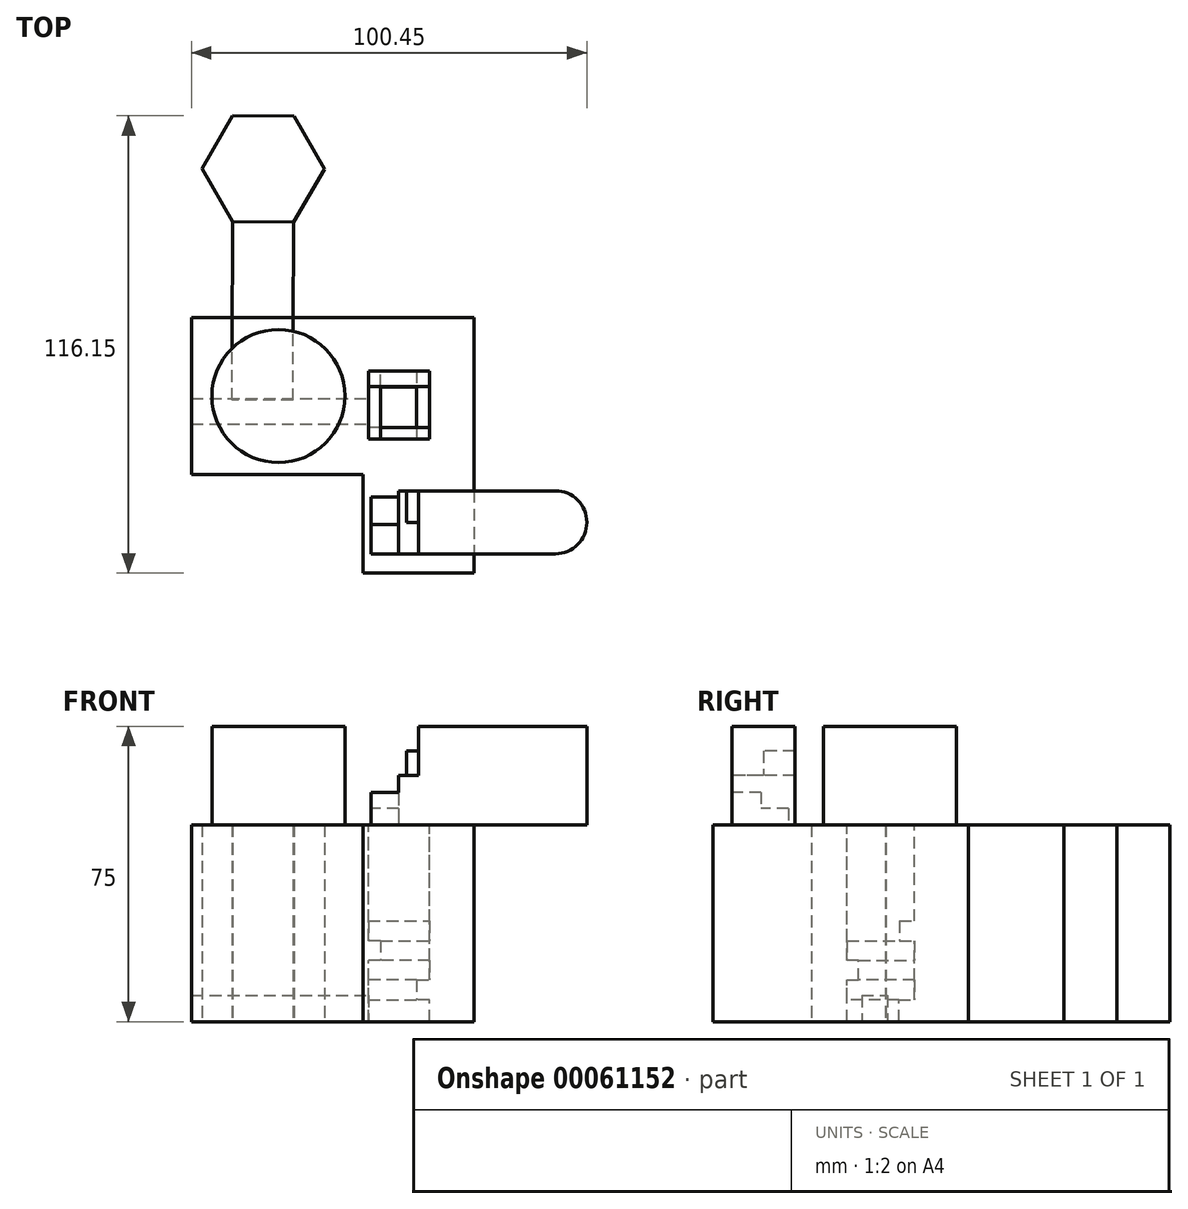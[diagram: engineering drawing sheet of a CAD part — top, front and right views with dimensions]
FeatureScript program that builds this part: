
annotation { "Feature Type Name" : "Feature", "Feature Type Description" : "" }
export const myFeature = defineFeature(function(context is Context, id is Id, definition is map)
    precondition{}
    {
        {
            var Q0;
            Q0=qCreatedBy(makeId("Top.planeOp"),FACE);
            var sketch = newSketch(context, id + "F0", { "sketchPlane" : qUnion([Q0])});
            skLineSegment(sketch, "E0.bottom", {"start": v(-25.79, 13.66) * mm, "end": v(46.05, 13.66) * mm});
            skLineSegment(sketch, "E0.top", {"start": v(-25.79, -26.25) * mm, "end": v(46.05, -26.25) * mm});
            skLineSegment(sketch, "E0.left", {"start": v(-25.79, 13.66) * mm, "end": v(-25.79, -26.25) * mm});
            skLineSegment(sketch, "E0.right", {"start": v(46.05, 13.66) * mm, "end": v(46.05, -26.25) * mm});
            skSolve(sketch);
        }
        {
            var Q0;
            Q0=qSketchRegion(id+"F0",true);
            extrude(context, id + "F1", {"entities" : qUnion([Q0]), "depth" : 25 * mm, "hasSecondDirection" : true, "secondDirectionOppositeDirection" : true, "secondDirectionDepth" : 25 * mm});
        }
        {
            var Q0;
            Q0=makeQuery(id+"F1.opExtrude","CAP_FACE",FACE,{"disambiguationData":[OSD([sQuery(id+"F0.wireOp",EDGE,"E0.bottom"),sQuery(id+"F0.wireOp",EDGE,"E0.top"),sQuery(id+"F0.wireOp",EDGE,"E0.left"),sQuery(id+"F0.wireOp",EDGE,"E0.right")])],"isStart":false});
            var sketch = newSketch(context, id + "F2", { "sketchPlane" : qUnion([Q0])});
            skLineSegment(sketch, "E1.bottom", {"start": v(19.18, 0) * mm, "end": v(34.73, 0) * mm});
            skLineSegment(sketch, "E1.top", {"start": v(19.18, -17.18) * mm, "end": v(34.73, -17.18) * mm});
            skLineSegment(sketch, "E1.left", {"start": v(19.18, 0) * mm, "end": v(19.18, -17.18) * mm});
            skLineSegment(sketch, "E1.right", {"start": v(34.73, 0) * mm, "end": v(34.73, -17.18) * mm});
            skSolve(sketch);
        }
        {
            var Q0;
            Q0=makeQuery(id+"F1.opExtrude","SWEPT_FACE",FACE,{"disambiguationData":[OSD([sQuery(id+"F0.wireOp",EDGE,"E0.top")])]});
            var sketch = newSketch(context, id + "F3", { "sketchPlane" : qUnion([Q0])});
            skLineSegment(sketch, "E2.bottom", {"start": v(46.05, 25) * mm, "end": v(17.8, 25) * mm});
            skLineSegment(sketch, "E2.top", {"start": v(46.05, -25) * mm, "end": v(17.8, -25) * mm});
            skLineSegment(sketch, "E2.left", {"start": v(46.05, 25) * mm, "end": v(46.05, -25) * mm});
            skLineSegment(sketch, "E2.right", {"start": v(17.8, 25) * mm, "end": v(17.8, -25) * mm});
            skSolve(sketch);
        }
        {
            var Q0;
            Q0=qSketchRegion(id+"F3",true);
            extrude(context, id + "F4", {"entities" : qUnion([Q0]), "operationType" : NewBodyOperationType.ADD, "depth" : 25 * mm});
        }
        {
            var Q0;
            Q0=makeQuery(id+"F2.imprint","IMPRINT",FACE,{"disambiguationData":[TD([[makeQuery(id+"F2.imprint","IMPRINT",EDGE,{"derivedFrom":sQuery(id+"F2.wireOp",EDGE,"E1.bottom")}),-1.0]])]});
            var Q1;
            Q1=qSketchRegion(id+"F2",true);
            extrude(context, id + "F5", {"entities" : qUnion([Q0, Q1]), "operationType" : NewBodyOperationType.REMOVE, "endBound" : BoundingType.THROUGH_ALL, "oppositeDirection" : true, "depth" : 25 * mm});
        }
        {
            var Q0;
            Q0=makeQuery(id+"F4.boolean.opBoolean","MERGE",FACE,{"derivedFrom":[makeQuery(id+"F1.opExtrude","CAP_FACE",FACE,{"disambiguationData":[OSD([sQuery(id+"F0.wireOp",EDGE,"E0.bottom"),sQuery(id+"F0.wireOp",EDGE,"E0.top"),sQuery(id+"F0.wireOp",EDGE,"E0.left"),sQuery(id+"F0.wireOp",EDGE,"E0.right")])],"isStart":false}),makeQuery(id+"F4.opExtrude","SWEPT_FACE",FACE,{"disambiguationData":[OSD([sQuery(id+"F3.wireOp",EDGE,"E2.bottom")])]})]});
            var sketch = newSketch(context, id + "F6", { "sketchPlane" : qUnion([Q0])});
            skCircle(sketch, "E3", {"center": v(-3.68, -6.3) * mm, "radius": 16.9 * mm});
            skSolve(sketch);
        }
        {
            var Q0;
            Q0=makeQuery(id+"F6.imprint","IMPRINT",FACE,{"disambiguationData":[TD([[makeQuery(id+"F6.imprint","IMPRINT",EDGE,{"derivedFrom":sQuery(id+"F6.wireOp",EDGE,"E3")}),1.0]])]});
            extrude(context, id + "F7", {"entities" : qUnion([Q0]), "operationType" : NewBodyOperationType.ADD, "depth" : 25 * mm});
        }
        {
            var Q0;
            Q0=makeQuery(id+"F4.boolean.opBoolean","MERGE",FACE,{"derivedFrom":[makeQuery(id+"F1.opExtrude","CAP_FACE",FACE,{"disambiguationData":[OSD([sQuery(id+"F0.wireOp",EDGE,"E0.bottom"),sQuery(id+"F0.wireOp",EDGE,"E0.top"),sQuery(id+"F0.wireOp",EDGE,"E0.left"),sQuery(id+"F0.wireOp",EDGE,"E0.right")])],"isStart":false}),makeQuery(id+"F4.opExtrude","SWEPT_FACE",FACE,{"disambiguationData":[OSD([sQuery(id+"F3.wireOp",EDGE,"E2.bottom")])]})]});
            var sketch = newSketch(context, id + "F8", { "sketchPlane" : qUnion([Q0])});
            skLineSegment(sketch, "E4", {"start": v(31.87, -30.37) * mm, "end": v(66.65, -30.37) * mm});
            skLineSegment(sketch, "E5", {"start": v(31.87, -46.4) * mm, "end": v(66.65, -46.4) * mm});
            skArc(sketch, "E6", {"start": v(66.65, -46.4) * mm, "mid": v(74.66, -38.38) * mm, "end": v(66.65, -30.37) * mm});
            skLineSegment(sketch, "E7", {"start": v(31.87, -46.4) * mm, "end": v(31.87, -30.37) * mm});
            skSolve(sketch);
        }
        {
            var Q0;
            {var subQ0=sQuery(id+"F8.wireOp",EDGE,"E6");Q0=makeQuery(id+"F8.imprint","IMPRINT",FACE,{"disambiguationData":[TD([[makeQuery(id+"F8.imprint","IMPRINT",EDGE,{"derivedFrom":subQ0}),1.0]])]});}
            var Q1;
            {var subQ0=sQuery(id+"F8.wireOp",EDGE,"E7");Q1=makeQuery(id+"F8.imprint","IMPRINT",FACE,{"disambiguationData":[TD([[makeQuery(id+"F8.imprint","IMPRINT",EDGE,{"derivedFrom":subQ0}),-1.0]])]});}
            extrude(context, id + "F9", {"entities" : qUnion([Q0, Q1]), "operationType" : NewBodyOperationType.ADD, "depth" : 25 * mm});
        }
        {
            var Q0;
            Q0=makeQuery(id+"F9.opExtrude","SWEPT_FACE",FACE,{"disambiguationData":[OSD([sQuery(id+"F8.wireOp",EDGE,"E7")])]});
            var sketch = newSketch(context, id + "F10", { "sketchPlane" : qUnion([Q0])});
            skLineSegment(sketch, "E8.bottom", {"start": v(30.37, 37.5) * mm, "end": v(46.4, 37.5) * mm});
            skLineSegment(sketch, "E8.top", {"start": v(30.37, 25) * mm, "end": v(46.4, 25) * mm});
            skLineSegment(sketch, "E8.left", {"start": v(30.37, 37.5) * mm, "end": v(30.37, 25) * mm});
            skLineSegment(sketch, "E8.right", {"start": v(46.4, 37.5) * mm, "end": v(46.4, 25) * mm});
            skSolve(sketch);
        }
        {
            var Q0;
            Q0=makeQuery(id+"F10.imprint","IMPRINT",FACE,{"disambiguationData":[TD([[makeQuery(id+"F10.imprint","IMPRINT",EDGE,{"derivedFrom":sQuery(id+"F10.wireOp",EDGE,"E8.bottom")}),-1.0]])]});
            extrude(context, id + "F11", {"entities" : qUnion([Q0]), "operationType" : NewBodyOperationType.ADD, "depth" : 5 * mm});
        }
        {
            var Q0;
            Q0=makeQuery(id+"F11.opExtrude","CAP_FACE",FACE,{"disambiguationData":[OSD([sQuery(id+"F10.wireOp",EDGE,"E8.bottom"),sQuery(id+"F10.wireOp",EDGE,"E8.top"),sQuery(id+"F10.wireOp",EDGE,"E8.left"),sQuery(id+"F10.wireOp",EDGE,"E8.right")])],"isStart":false});
            var sketch = newSketch(context, id + "F12", { "sketchPlane" : qUnion([Q0])});
            skLineSegment(sketch, "E9.bottom", {"start": v(38.97, 33.28) * mm, "end": v(46.4, 33.28) * mm});
            skLineSegment(sketch, "E9.top", {"start": v(38.97, 25) * mm, "end": v(46.4, 25) * mm});
            skLineSegment(sketch, "E9.left", {"start": v(38.97, 33.28) * mm, "end": v(38.97, 25) * mm});
            skLineSegment(sketch, "E9.right", {"start": v(46.4, 33.28) * mm, "end": v(46.4, 25) * mm});
            skSolve(sketch);
        }
        {
            var Q0;
            Q0=qSketchRegion(id+"F12",true);
            extrude(context, id + "F13", {"entities" : qUnion([Q0]), "operationType" : NewBodyOperationType.ADD, "depth" : 7 * mm});
        }
        {
            var Q0;
            Q0=makeQuery(id+"F13.opExtrude","SWEPT_FACE",FACE,{"disambiguationData":[OSD([sQuery(id+"F12.wireOp",EDGE,"E9.left")])]});
            var sketch = newSketch(context, id + "F14", { "sketchPlane" : qUnion([Q0])});
            skLineSegment(sketch, "E10.bottom", {"start": v(-26.87, 29.14) * mm, "end": v(-19.87, 29.14) * mm});
            skLineSegment(sketch, "E10.top", {"start": v(-26.87, 25) * mm, "end": v(-19.87, 25) * mm});
            skLineSegment(sketch, "E10.left", {"start": v(-26.87, 29.14) * mm, "end": v(-26.87, 25) * mm});
            skLineSegment(sketch, "E10.right", {"start": v(-19.87, 29.14) * mm, "end": v(-19.87, 25) * mm});
            skSolve(sketch);
        }
        {
            var Q0;
            Q0=qSketchRegion(id+"F14",true);
            extrude(context, id + "F15", {"entities" : qUnion([Q0]), "operationType" : NewBodyOperationType.ADD, "depth" : 7 * mm});
        }
        {
            var Q0;
            Q0=makeQuery(id+"F9.opExtrude","SWEPT_FACE",FACE,{"disambiguationData":[OSD([sQuery(id+"F8.wireOp",EDGE,"E7")])]});
            var sketch = newSketch(context, id + "F16", { "sketchPlane" : qUnion([Q0])});
            skLineSegment(sketch, "E11.bottom", {"start": v(30.37, 43.75) * mm, "end": v(38.38, 43.75) * mm});
            skLineSegment(sketch, "E11.top", {"start": v(30.37, 37.5) * mm, "end": v(38.38, 37.5) * mm});
            skLineSegment(sketch, "E11.left", {"start": v(30.37, 43.75) * mm, "end": v(30.37, 37.5) * mm});
            skLineSegment(sketch, "E11.right", {"start": v(38.38, 43.75) * mm, "end": v(38.38, 37.5) * mm});
            skSolve(sketch);
        }
        {
            var Q0;
            Q0=qSketchRegion(id+"F16",true);
            extrude(context, id + "F17", {"entities" : qUnion([Q0]), "operationType" : NewBodyOperationType.ADD, "depth" : 3 * mm});
        }
        {
            var Q0;
            Q0=makeQuery(id+"F5.boolean.opBoolean","COPY",FACE,{"derivedFrom":makeQuery(id+"F5.opExtrude","SWEPT_FACE",FACE,{"disambiguationData":[OSD([sQuery(id+"F2.wireOp",EDGE,"E1.bottom")])]})});
            var sketch = newSketch(context, id + "F18", { "sketchPlane" : qUnion([Q0])});
            skLineSegment(sketch, "E12.bottom", {"start": v(19.18, -25) * mm, "end": v(34.73, -25) * mm});
            skLineSegment(sketch, "E12.top", {"start": v(19.18, -19.44) * mm, "end": v(34.73, -19.44) * mm});
            skLineSegment(sketch, "E12.left", {"start": v(19.18, -25) * mm, "end": v(19.18, -19.44) * mm});
            skLineSegment(sketch, "E12.right", {"start": v(34.73, -25) * mm, "end": v(34.73, -19.44) * mm});
            skSolve(sketch);
        }
        {
            var Q0;
            Q0=makeQuery(id+"F18.imprint","IMPRINT",FACE,{"disambiguationData":[TD([[makeQuery(id+"F18.imprint","IMPRINT",EDGE,{"derivedFrom":sQuery(id+"F18.wireOp",EDGE,"E12.bottom")}),1.0]])]});
            extrude(context, id + "F19", {"entities" : qUnion([Q0]), "operationType" : NewBodyOperationType.ADD, "depth" : 4 * mm});
        }
        {
            var Q0;
            Q0=makeQuery(id+"F19.opExtrude","SWEPT_FACE",FACE,{"disambiguationData":[OSD([sQuery(id+"F18.wireOp",EDGE,"E12.top")])]});
            var sketch = newSketch(context, id + "F20", { "sketchPlane" : qUnion([Q0])});
            skLineSegment(sketch, "E13.bottom", {"start": v(34.73, 0) * mm, "end": v(31.43, 0) * mm});
            skLineSegment(sketch, "E13.top", {"start": v(34.73, -17.48) * mm, "end": v(31.43, -17.48) * mm});
            skLineSegment(sketch, "E13.left", {"start": v(34.73, 0) * mm, "end": v(34.73, -17.48) * mm});
            skLineSegment(sketch, "E13.right", {"start": v(31.43, 0) * mm, "end": v(31.43, -17.48) * mm});
            skSolve(sketch);
        }
        {
            var Q0;
            Q0=qSketchRegion(id+"F20",true);
            extrude(context, id + "F21", {"entities" : qUnion([Q0]), "operationType" : NewBodyOperationType.ADD, "depth" : 5 * mm});
        }
        {
            var Q0;
            Q0=makeQuery(id+"F21.opExtrude","CAP_FACE",FACE,{"disambiguationData":[OSD([sQuery(id+"F20.wireOp",EDGE,"E13.bottom"),sQuery(id+"F20.wireOp",EDGE,"E13.top"),sQuery(id+"F20.wireOp",EDGE,"E13.left"),sQuery(id+"F20.wireOp",EDGE,"E13.right")])],"isStart":false});
            var sketch = newSketch(context, id + "F22", { "sketchPlane" : qUnion([Q0])});
            skLineSegment(sketch, "E14.bottom", {"start": v(34.73, -14.24) * mm, "end": v(19.11, -14.24) * mm});
            skLineSegment(sketch, "E14.top", {"start": v(34.73, -17.18) * mm, "end": v(19.11, -17.18) * mm});
            skLineSegment(sketch, "E14.left", {"start": v(34.73, -14.24) * mm, "end": v(34.73, -17.18) * mm});
            skLineSegment(sketch, "E14.right", {"start": v(19.11, -14.24) * mm, "end": v(19.11, -17.18) * mm});
            skSolve(sketch);
        }
        {
            var Q0;
            {var subQ0=sQuery(id+"F22.wireOp",EDGE,"E14.right");Q0=makeQuery(id+"F22.imprint","IMPRINT",FACE,{"disambiguationData":[TD([[makeQuery(id+"F22.imprint","IMPRINT",EDGE,{"derivedFrom":subQ0}),1.0]])]});}
            var Q1;
            {var subQ0=sQuery(id+"F22.wireOp",EDGE,"E14.left");Q1=makeQuery(id+"F22.imprint","IMPRINT",FACE,{"disambiguationData":[TD([[makeQuery(id+"F22.imprint","IMPRINT",EDGE,{"derivedFrom":subQ0}),-1.0]])]});}
            extrude(context, id + "F23", {"entities" : qUnion([Q0, Q1]), "operationType" : NewBodyOperationType.ADD, "depth" : 5 * mm});
        }
        {
            var Q0;
            Q0=makeQuery(id+"F23.opExtrude","CAP_FACE",FACE,{"disambiguationData":[OSD([sQuery(id+"F22.wireOp",EDGE,"E14.bottom"),sQuery(id+"F22.wireOp",EDGE,"E14.top"),sQuery(id+"F22.wireOp",EDGE,"E14.left"),sQuery(id+"F22.wireOp",EDGE,"E14.right")])],"isStart":false});
            var sketch = newSketch(context, id + "F24", { "sketchPlane" : qUnion([Q0])});
            skLineSegment(sketch, "E15.bottom", {"start": v(22.25, -17.18) * mm, "end": v(19.18, -17.18) * mm});
            skLineSegment(sketch, "E15.top", {"start": v(22.25, 0) * mm, "end": v(19.18, 0) * mm});
            skLineSegment(sketch, "E15.left", {"start": v(22.25, -17.18) * mm, "end": v(22.25, 0) * mm});
            skLineSegment(sketch, "E15.right", {"start": v(19.18, -17.18) * mm, "end": v(19.18, 0) * mm});
            skSolve(sketch);
        }
        {
            var Q0;
            {var subQ0=sQuery(id+"F24.wireOp",EDGE,"E15.top");Q0=makeQuery(id+"F24.imprint","IMPRINT",FACE,{"disambiguationData":[TD([[makeQuery(id+"F24.imprint","IMPRINT",EDGE,{"derivedFrom":subQ0}),1.0]])]});}
            var Q1;
            {var subQ0=sQuery(id+"F24.wireOp",EDGE,"E15.bottom");Q1=makeQuery(id+"F24.imprint","IMPRINT",FACE,{"disambiguationData":[TD([[makeQuery(id+"F24.imprint","IMPRINT",EDGE,{"derivedFrom":subQ0}),-1.0]])]});}
            extrude(context, id + "F25", {"entities" : qUnion([Q0, Q1]), "operationType" : NewBodyOperationType.ADD, "depth" : 5 * mm});
        }
        {
            var Q0;
            Q0=makeQuery(id+"F25.opExtrude","CAP_FACE",FACE,{"disambiguationData":[OSD([sQuery(id+"F24.wireOp",EDGE,"E15.bottom"),sQuery(id+"F24.wireOp",EDGE,"E15.top"),sQuery(id+"F24.wireOp",EDGE,"E15.left"),sQuery(id+"F24.wireOp",EDGE,"E15.right")])],"isStart":false});
            var sketch = newSketch(context, id + "F26", { "sketchPlane" : qUnion([Q0])});
            skLineSegment(sketch, "E16.bottom", {"start": v(19.18, -3.84) * mm, "end": v(34.88, -3.84) * mm});
            skLineSegment(sketch, "E16.top", {"start": v(19.18, 0) * mm, "end": v(34.88, 0) * mm});
            skLineSegment(sketch, "E16.left", {"start": v(19.18, -3.84) * mm, "end": v(19.18, 0) * mm});
            skLineSegment(sketch, "E16.right", {"start": v(34.88, -3.84) * mm, "end": v(34.88, 0) * mm});
            skSolve(sketch);
        }
        {
            var Q0;
            {var subQ0=sQuery(id+"F26.wireOp",EDGE,"E16.right");Q0=makeQuery(id+"F26.imprint","IMPRINT",FACE,{"disambiguationData":[TD([[makeQuery(id+"F26.imprint","IMPRINT",EDGE,{"derivedFrom":subQ0}),1.0]])]});}
            var Q1;
            {var subQ0=sQuery(id+"F26.wireOp",EDGE,"E16.left");Q1=makeQuery(id+"F26.imprint","IMPRINT",FACE,{"disambiguationData":[TD([[makeQuery(id+"F26.imprint","IMPRINT",EDGE,{"derivedFrom":subQ0}),-1.0]])]});}
            extrude(context, id + "F27", {"entities" : qUnion([Q0, Q1]), "operationType" : NewBodyOperationType.ADD, "depth" : 5 * mm});
        }
        {
            var Q0;
            Q0=makeQuery(id+"F25.boolean.opBoolean","SPLIT",FACE,{"disambiguationData":[TD([makeQuery(id+"F4.opExtrude","SWEPT_FACE",FACE,{"disambiguationData":[OSD([sQuery(id+"F3.wireOp",EDGE,"E2.top")])]})])],"derivedFrom":makeQuery(id+"F5.boolean.opBoolean","COPY",FACE,{"derivedFrom":makeQuery(id+"F5.opExtrude","SWEPT_FACE",FACE,{"disambiguationData":[OSD([sQuery(id+"F2.wireOp",EDGE,"E1.left")])]})})});
            var sketch = newSketch(context, id + "F28", { "sketchPlane" : qUnion([Q0])});
            skLineSegment(sketch, "E17.bottom", {"start": v(-13.38, -18.35) * mm, "end": v(-6.94, -18.35) * mm});
            skLineSegment(sketch, "E17.top", {"start": v(-13.38, -25) * mm, "end": v(-6.94, -25) * mm});
            skLineSegment(sketch, "E17.left", {"start": v(-13.38, -18.35) * mm, "end": v(-13.38, -25) * mm});
            skLineSegment(sketch, "E17.right", {"start": v(-6.94, -18.35) * mm, "end": v(-6.94, -25) * mm});
            skSolve(sketch);
        }
        {
            var Q0;
            Q0=makeQuery(id+"F28.imprint","IMPRINT",FACE,{"disambiguationData":[TD([[makeQuery(id+"F28.imprint","IMPRINT",EDGE,{"derivedFrom":sQuery(id+"F28.wireOp",EDGE,"E17.bottom")}),-1.0]])]});
            extrude(context, id + "F29", {"entities" : qUnion([Q0]), "operationType" : NewBodyOperationType.REMOVE, "endBound" : BoundingType.THROUGH_ALL, "oppositeDirection" : true, "depth" : 25 * mm});
        }
        {
            var Q0;
            Q0=makeQuery(id+"F29.boolean.opBoolean","COPY",FACE,{"derivedFrom":makeQuery(id+"F29.opExtrude","SWEPT_FACE",FACE,{"disambiguationData":[OSD([sQuery(id+"F28.wireOp",EDGE,"E17.bottom")])]})});
            var sketch = newSketch(context, id + "F30", { "sketchPlane" : qUnion([Q0])});
            skLineSegment(sketch, "E18.bottom", {"start": v(-13.26, 13.38) * mm, "end": v(-7.58, 13.38) * mm});
            skLineSegment(sketch, "E18.top", {"start": v(-13.26, 6.94) * mm, "end": v(-7.58, 6.94) * mm});
            skLineSegment(sketch, "E18.left", {"start": v(-13.26, 13.38) * mm, "end": v(-13.26, 6.94) * mm});
            skLineSegment(sketch, "E18.right", {"start": v(-7.58, 13.38) * mm, "end": v(-7.58, 6.94) * mm});
            skSolve(sketch);
        }
        {
            var Q0;
            Q0=qCreatedBy(makeId("Top.planeOp"),FACE);
            var sketch = newSketch(context, id + "F31", { "sketchPlane" : qUnion([Q0])});
            skCircle(sketch, "E19.cCircle", {"center": v(-7.58, 51.41) * mm, "radius": 13.46 * mm, "construction": true});
            skLineSegment(sketch, "E19.0", {"start": v(7.97, 51.37) * mm, "end": v(0.15, 37.93) * mm});
            skLineSegment(sketch, "E19.1", {"start": v(0.15, 37.93) * mm, "end": v(-15.39, 37.98) * mm});
            skLineSegment(sketch, "E19.2", {"start": v(-15.39, 37.98) * mm, "end": v(-23.12, 51.46) * mm});
            skLineSegment(sketch, "E19.3", {"start": v(-23.12, 51.46) * mm, "end": v(-15.3, 64.9) * mm});
            skLineSegment(sketch, "E19.4", {"start": v(-15.3, 64.9) * mm, "end": v(0.23, 64.85) * mm});
            skLineSegment(sketch, "E19.5", {"start": v(0.23, 64.85) * mm, "end": v(7.97, 51.37) * mm});
            skPoint(sketch, "E19.0.midPoint", {"position": v(4.06, 44.65) * mm});
            skSolve(sketch);
        }
        {
            var Q0;
            Q0=makeQuery(id+"F31.imprint","IMPRINT",FACE,{"disambiguationData":[TD([[makeQuery(id+"F31.imprint","IMPRINT",EDGE,{"derivedFrom":sQuery(id+"F31.wireOp",EDGE,"E19.0")}),-1.0]])]});
            extrude(context, id + "F32", {"entities" : qUnion([Q0]), "depth" : 25 * mm, "hasSecondDirection" : true, "secondDirectionOppositeDirection" : true, "secondDirectionDepth" : 25 * mm});
        }
        {
            var Q0;
            Q0=makeQuery(id+"F32.opExtrude","SWEPT_FACE",FACE,{"disambiguationData":[OSD([sQuery(id+"F31.wireOp",EDGE,"E19.1")])]});
            extrude(context, id + "F33", {"entities" : qUnion([Q0]), "depth" : 45.3 * mm});
        }
    });
